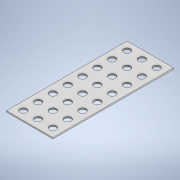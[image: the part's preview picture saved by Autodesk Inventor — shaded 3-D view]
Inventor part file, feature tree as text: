
AUTODESK INVENTOR PART (.ipt)
format: ipt  version: 2020 (Build 240168000, 168)  size: 169,984 bytes
history: native  units: in
note: dims shown in document units (in); Inventor stores cm internally (conversion verified against a paired STEP export)
features: extrude x1, sketch x1
ambient origin geometry x8: Origin, YZ Plane, XZ Plane, XY Plane, X Axis, Y Axis, Z Axis, Center Point
bodies: Solid1 (feature_tree)
feature tree (2):
  extrude  "Extrusion1"  Depth=4.353in
  sketch  "Sketch1"  dims[d0=11.293in d1=4.353in d2=0.64in d3=3.1496in d5=1.388in d6=1.1811in d8=1.388in d11=0.7885in d12=0.7885in d13=0.125in d14=0.0in]
